# Revit family: Plumbing-Fix_Faucet_Stern_Touch-BRE
name_source: partatom
category: Plumbing Fixtures
units: mm (PartAtom-declared; Revit-internal decimal feet)

## family parameters
Classification Number = 23.45.55.14
Cut with Voids When Loaded = No
Enable Cutting in Views = No
Host = Face
Maintain Annotation Orientation = No
Part Type = Normal
Room Calculation Point = No
Round Connector Dimension = Use Diameter
Shared = No

## types (2) — shared parameters
Assembly Code = D2010300
Available Options = as Specified
Body Construction = Brass
CW Connection = Yes
CWFU = 1
Default Elevation = 0' - 0"
Description = Stern Deck Mounted Faucet - Touch BRE as Specified
HW Connection = Yes
HWFU = 1
Keynote = 22 40 00
Manufacturer = Stern Engineering
Manufacturer Website = http://www.sternfaucets.com
Model = Touch BRE
Operating Pressure Range = 7.26 - 116 PSI  ;  0.5 - 8 bar
Operating Temperature Range = Up to 149 F / 65 C
Piping_Flow = 1 GPM
Piping_Inlet Diameter = 1"
Power Supply = 9V Transformer
Product Data = http://www.arcat.com
Product Features = Security Shut Off Timer  ;  Water Temperature Indicator
Revision = R1_2018-04
Sales Information = http://www.sternfaucets.com
Spout Height = 0' - 3 3/8"
Spout Reach = 0' - 3 3/4"
Standards Conformance = Lead Free
Type Comments = as Specified
URL = http://www.sternfaucets.com
Unit Height = 0' - 5 1/8"
Unit Width = 0' - 2"
Vent Connection = No
Warranty Duration (Years) = 2
Waste Connection = No
zero-valued in all types: Cost, Expected Lifespan (Years), Maintenance Schedule (Months), WFU

## type names (no varying parameters)
- 1.32 GPM
- 0.5 GPM

## geometry (parser evidence)
native form markers: Sweep x2
no freeform markers — native parametric forms only
